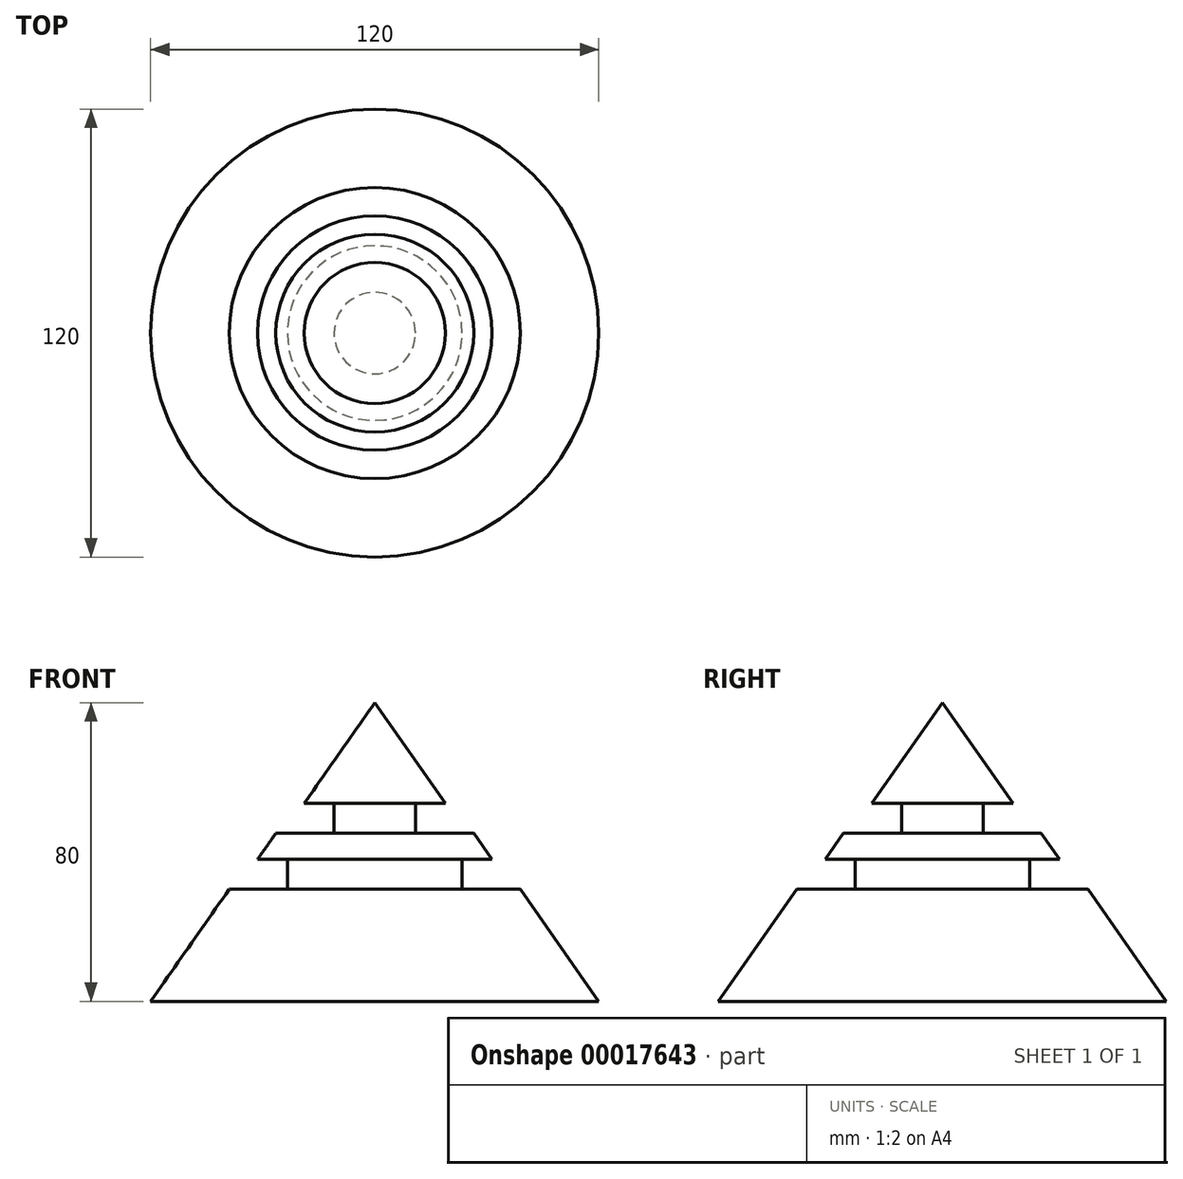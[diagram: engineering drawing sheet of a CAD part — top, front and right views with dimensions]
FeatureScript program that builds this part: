
annotation { "Feature Type Name" : "Feature", "Feature Type Description" : "" }
export const myFeature = defineFeature(function(context is Context, id is Id, definition is map)
    precondition{}
    {
        {
            var Q0;
            Q0=qCreatedBy(makeId("Front.planeOp"),FACE);
            var sketch = newSketch(context, id + "F0", { "sketchPlane" : qUnion([Q0])});
            skLineSegment(sketch, "E0", {"start": v(0, 0) * mm, "end": v(0, 80) * mm});
            skLineSegment(sketch, "E1", {"start": v(0, 80) * mm, "end": v(18.9, 53) * mm});
            skLineSegment(sketch, "E2", {"start": v(18.9, 53) * mm, "end": v(10.9, 53) * mm});
            skLineSegment(sketch, "E3", {"start": v(10.9, 53) * mm, "end": v(10.9, 45) * mm});
            skLineSegment(sketch, "E4", {"start": v(10.9, 45) * mm, "end": v(26.5, 45) * mm});
            skLineSegment(sketch, "E5", {"start": v(26.5, 45) * mm, "end": v(31.4, 38) * mm});
            skLineSegment(sketch, "E6", {"start": v(31.4, 38) * mm, "end": v(23.4, 38) * mm});
            skLineSegment(sketch, "E7", {"start": v(23.4, 38) * mm, "end": v(23.4, 30) * mm});
            skLineSegment(sketch, "E8", {"start": v(23.4, 30) * mm, "end": v(39, 30) * mm});
            skLineSegment(sketch, "E9", {"start": v(39, 30) * mm, "end": v(60, 0) * mm});
            skLineSegment(sketch, "E10", {"start": v(60, 0) * mm, "end": v(0, 0) * mm});
            skSolve(sketch);
        }
        {
            var Q0;
            Q0=makeQuery(id+"F0.imprint","IMPRINT",FACE,{"disambiguationData":[TD([[makeQuery(id+"F0.imprint","IMPRINT",EDGE,{"derivedFrom":sQuery(id+"F0.wireOp",EDGE,"E0")}),-1.0]])]});
            var Q1;
            Q1=sQuery(id+"F0.wireOp",EDGE,"E0");
            revolve(context, id + "F1", {"entities" : qUnion([Q0]), "axis" : qUnion([Q1]), "revolveType" : RevolveType.FULL});
        }
    });
